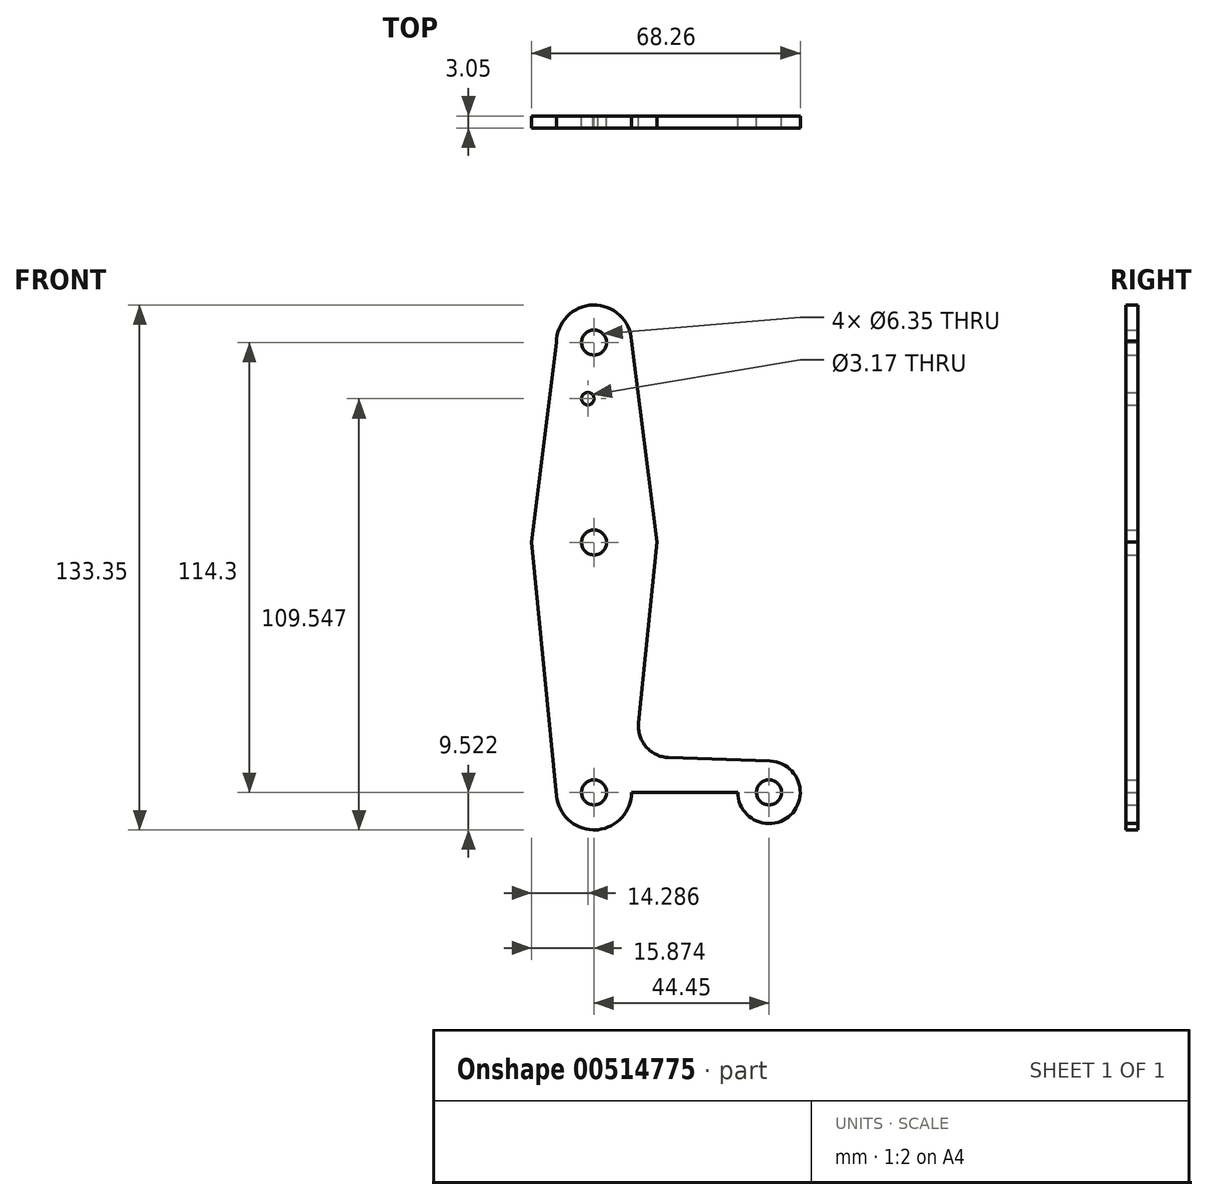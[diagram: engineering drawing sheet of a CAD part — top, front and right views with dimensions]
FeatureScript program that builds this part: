
annotation { "Feature Type Name" : "Feature", "Feature Type Description" : "" }
export const myFeature = defineFeature(function(context is Context, id is Id, definition is map)
    precondition{}
    {
        {
            var Q0;
            Q0=qCreatedBy(makeId("Front.planeOp"),FACE);
            var sketch = newSketch(context, id + "F0", { "sketchPlane" : qUnion([Q0])});
            skCircle(sketch, "E0", {"center": v(21.17, 118.46) * mm, "radius": 9.53 * mm});
            skLineSegment(sketch, "E1", {"start": v(21.17, 118.46) * mm, "end": v(21.17, 67.66) * mm});
            skCircle(sketch, "E2", {"center": v(21.17, 67.66) * mm, "radius": 15.88 * mm});
            skLineSegment(sketch, "E3", {"start": v(21.17, 67.66) * mm, "end": v(21.17, 4.16) * mm});
            skCircle(sketch, "E4", {"center": v(21.17, 4.16) * mm, "radius": 9.53 * mm});
            skLineSegment(sketch, "E5", {"start": v(21.17, 4.16) * mm, "end": v(65.62, 4.16) * mm});
            skCircle(sketch, "E6", {"center": v(65.62, 4.16) * mm, "radius": 7.94 * mm});
            skLineSegment(sketch, "E7", {"start": v(5.3, 67.72) * mm, "end": v(11.7, 3.22) * mm});
            skLineSegment(sketch, "E8", {"start": v(11.65, 118.4) * mm, "end": v(5.3, 67.72) * mm});
            skLineSegment(sketch, "E9", {"start": v(30.7, 118.86) * mm, "end": v(37.17, 67.72) * mm});
            skLineSegment(sketch, "E10", {"start": v(40.12, 13.01) * mm, "end": v(65.9, 12.1) * mm});
            skLineSegment(sketch, "E11", {"start": v(20.85, -5.36) * mm, "end": v(65.9, -3.77) * mm});
            skCircle(sketch, "E12", {"center": v(19.59, 104.19) * mm, "radius": 1.59 * mm});
            skLineSegment(sketch, "E13", {"start": v(32.49, 21.76) * mm, "end": v(37.17, 67.72) * mm});
            skCircle(sketch, "E14", {"center": v(21.17, 67.66) * mm, "radius": 3.18 * mm});
            skCircle(sketch, "E15", {"center": v(21.17, 118.46) * mm, "radius": 3.18 * mm});
            skCircle(sketch, "E16", {"center": v(21.17, 4.16) * mm, "radius": 3.18 * mm});
            skCircle(sketch, "E17", {"center": v(65.62, 4.16) * mm, "radius": 3.18 * mm});
            skArc(sketch, "E18.filletArc", {"start": v(32.49, 21.76) * mm, "mid": v(34.4, 15.73) * mm, "end": v(40.12, 13.01) * mm});
            skSolve(sketch);
        }
        {
            var Q0;
            Q0=makeQuery(id+"F0.imprint","IMPRINT",FACE,{"disambiguationData":[TD([[makeQuery(id+"F0.imprint","IMPRINT",EDGE,{"derivedFrom":sQuery(id+"F0.wireOp",EDGE,"E17")}),-1.0]])]});
            var Q1;
            {var subQ9=sQuery(id+"F0.wireOp",EDGE,"E10");Q1=makeQuery(id+"F0.imprint","IMPRINT",FACE,{"disambiguationData":[TD([[makeQuery(id+"F0.imprint","IMPRINT",EDGE,{"derivedFrom":subQ9}),-1.0]])]});}
            var Q2;
            {var subQ0=sQuery(id+"F0.wireOp",EDGE,"E11");var subQ1=sQuery(id+"F0.wireOp",EDGE,"E4");var subQ2=makeQuery(id+"F0.imprint","INTERSECT",VERTEX,{"disambiguationData":[OD(1.0)],"derivedFrom":[subQ1,subQ0]});Q2=makeQuery(id+"F0.imprint","IMPRINT",FACE,{"disambiguationData":[TD([[makeQuery(id+"F0.imprint","IMPRINT",EDGE,{"disambiguationData":[TD([[subQ2,-1.0]])],"derivedFrom":subQ1}),-1.0]])]});}
            var Q3;
            {var subQ1=sQuery(id+"F0.wireOp",EDGE,"E4");var subQ6=sQuery(id+"F0.wireOp",EDGE,"E3");var subQ11=makeQuery(id+"F0.imprint","INTERSECT",VERTEX,{"derivedFrom":[subQ6,subQ1]});Q3=makeQuery(id+"F0.imprint","IMPRINT",FACE,{"disambiguationData":[TD([[makeQuery(id+"F0.imprint","IMPRINT",EDGE,{"disambiguationData":[TD([[subQ11,-1.0]])],"derivedFrom":subQ6}),-1.0]])]});}
            var Q4;
            {var subQ0=sQuery(id+"F0.wireOp",EDGE,"E4");var subQ1=sQuery(id+"F0.wireOp",EDGE,"E3");var subQ2=makeQuery(id+"F0.imprint","INTERSECT",VERTEX,{"derivedFrom":[subQ1,subQ0]});Q4=makeQuery(id+"F0.imprint","IMPRINT",FACE,{"disambiguationData":[TD([[makeQuery(id+"F0.imprint","IMPRINT",EDGE,{"disambiguationData":[TD([[subQ2,-1.0]])],"derivedFrom":subQ1}),1.0]])]});}
            var Q5;
            {var subQ0=sQuery(id+"F0.wireOp",EDGE,"E7");var subQ1=sQuery(id+"F0.wireOp",EDGE,"E2");var subQ2=makeQuery(id+"F0.imprint","INTERSECT",VERTEX,{"derivedFrom":[subQ1,subQ0]});Q5=makeQuery(id+"F0.imprint","IMPRINT",FACE,{"disambiguationData":[TD([[makeQuery(id+"F0.imprint","IMPRINT",EDGE,{"disambiguationData":[TD([[subQ2,-1.0]])],"derivedFrom":subQ1}),-1.0]])]});}
            var Q6;
            {var subQ1=sQuery(id+"F0.wireOp",EDGE,"E2");var subQ9=sQuery(id+"F0.wireOp",EDGE,"E1");var subQ10=makeQuery(id+"F0.imprint","INTERSECT",VERTEX,{"derivedFrom":[subQ9,subQ1]});Q6=makeQuery(id+"F0.imprint","IMPRINT",FACE,{"disambiguationData":[TD([[makeQuery(id+"F0.imprint","IMPRINT",EDGE,{"disambiguationData":[TD([[subQ10,-1.0]])],"derivedFrom":subQ9}),-1.0]])]});}
            var Q7;
            {var subQ1=sQuery(id+"F0.wireOp",EDGE,"E2");var subQ6=sQuery(id+"F0.wireOp",EDGE,"E1");var subQ7=makeQuery(id+"F0.imprint","INTERSECT",VERTEX,{"derivedFrom":[subQ6,subQ1]});Q7=makeQuery(id+"F0.imprint","IMPRINT",FACE,{"disambiguationData":[TD([[makeQuery(id+"F0.imprint","IMPRINT",EDGE,{"disambiguationData":[TD([[subQ7,-1.0]])],"derivedFrom":subQ6}),1.0]])]});}
            var Q8;
            {var subQ4=sQuery(id+"F0.wireOp",EDGE,"E0");var subQ6=sQuery(id+"F0.wireOp",EDGE,"E9");var subQ8=makeQuery(id+"F0.imprint","INTERSECT",VERTEX,{"derivedFrom":[subQ4,subQ6]});Q8=makeQuery(id+"F0.imprint","IMPRINT",FACE,{"disambiguationData":[TD([[makeQuery(id+"F0.imprint","IMPRINT",EDGE,{"disambiguationData":[TD([[subQ8,1.0]])],"derivedFrom":subQ4}),-1.0]])]});}
            var Q9;
            {var subQ0=sQuery(id+"F0.wireOp",EDGE,"E12");Q9=makeQuery(id+"F0.imprint","IMPRINT",FACE,{"disambiguationData":[TD([[makeQuery(id+"F0.imprint","IMPRINT",EDGE,{"derivedFrom":subQ0}),-1.0]])]});}
            var Q10;
            Q10=makeQuery(id+"F0.imprint","IMPRINT",FACE,{"disambiguationData":[TD([[makeQuery(id+"F0.imprint","IMPRINT",EDGE,{"derivedFrom":sQuery(id+"F0.wireOp",EDGE,"E15")}),-1.0]])]});
            extrude(context, id + "F1", {"entities" : qUnion([Q0, Q1, Q2, Q3, Q4, Q5, Q6, Q7, Q8, Q9, Q10]), "depth" : 3.05 * mm, "offsetDistance" : 25.4 * mm});
        }
    });
